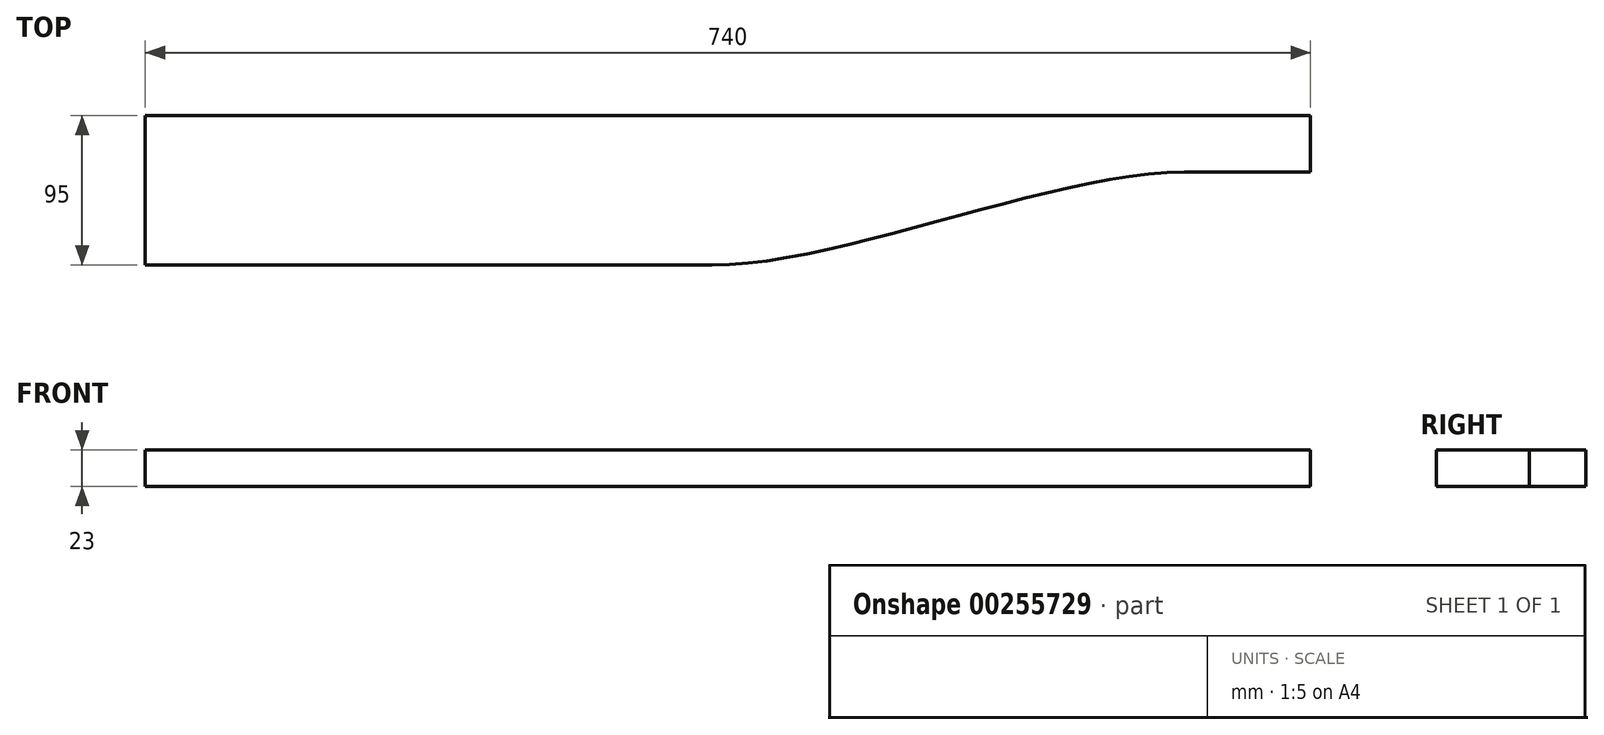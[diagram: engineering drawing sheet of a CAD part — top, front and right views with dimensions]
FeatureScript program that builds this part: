
annotation { "Feature Type Name" : "Feature", "Feature Type Description" : "" }
export const myFeature = defineFeature(function(context is Context, id is Id, definition is map)
    precondition{}
    {
        {
            var Q0;
            Q0=qCreatedBy(makeId("Top.planeOp"),FACE);
            var sketch = newSketch(context, id + "F0", { "sketchPlane" : qUnion([Q0])});
            skLineSegment(sketch, "E0.bottom", {"start": v(0, 0) * mm, "end": v(740, 0) * mm, "construction": true});
            skLineSegment(sketch, "E0.top", {"start": v(0, 95) * mm, "end": v(740, 95) * mm, "construction": true});
            skLineSegment(sketch, "E0.left", {"start": v(0, 0) * mm, "end": v(0, 95) * mm, "construction": true});
            skLineSegment(sketch, "E0.right", {"start": v(740, 0) * mm, "end": v(740, 95) * mm, "construction": true});
            skLineSegment(sketch, "E1.bottom", {"start": v(740, 59) * mm, "end": v(710, 59) * mm, "construction": true});
            skLineSegment(sketch, "E1.top", {"start": v(740, 24) * mm, "end": v(710, 24) * mm, "construction": true});
            skLineSegment(sketch, "E1.left", {"start": v(740, 59) * mm, "end": v(740, 24) * mm, "construction": true});
            skLineSegment(sketch, "E1.right", {"start": v(710, 59) * mm, "end": v(710, 24) * mm, "construction": true});
            skSolve(sketch);
        }
        {
            var Q0;
            Q0=qCreatedBy(makeId("Top.planeOp"),FACE);
            var sketch = newSketch(context, id + "F1", { "sketchPlane" : qUnion([Q0])});
            skLineSegment(sketch, "E2.bottom", {"start": v(0, 95) * mm, "end": v(740, 95) * mm});
            skLineSegment(sketch, "E2.left", {"start": v(0, 95) * mm, "end": v(0, 0) * mm});
            skFitSpline(sketch, "E3", {"points": [v(660, 59) * mm, v(360, 0) * mm], "startDerivative": vector(-251.58, 0) * mm, "endDerivative": vector(-248.68, 0) * mm});
            skLineSegment(sketch, "E4.0", {"start": v(740, 0) * mm, "end": v(740, 95) * mm, "construction": true});
            skPoint(sketch, "E5.0", {"position": v(710, 59) * mm});
            skPoint(sketch, "E6.0", {"position": v(740, 59) * mm});
            skLineSegment(sketch, "E7.top", {"start": v(660, 59) * mm, "end": v(740, 59) * mm});
            skLineSegment(sketch, "E7.right", {"start": v(740, 95) * mm, "end": v(740, 59) * mm});
            skLineSegment(sketch, "E8", {"start": v(0, 0) * mm, "end": v(360, 0) * mm});
            skSolve(sketch);
        }
        {
            var Q0;
            {var subQ1=sQuery(id+"F1.wireOp",EDGE,"E2.bottom");Q0=makeQuery(id+"F1.imprint","IMPRINT",FACE,{"disambiguationData":[TD([[makeQuery(id+"F1.imprint","IMPRINT",EDGE,{"derivedFrom":subQ1}),-1.0]])]});}
            extrude(context, id + "F2", {"entities" : qUnion([Q0]), "depth" : 23 * mm});
        }
    });
